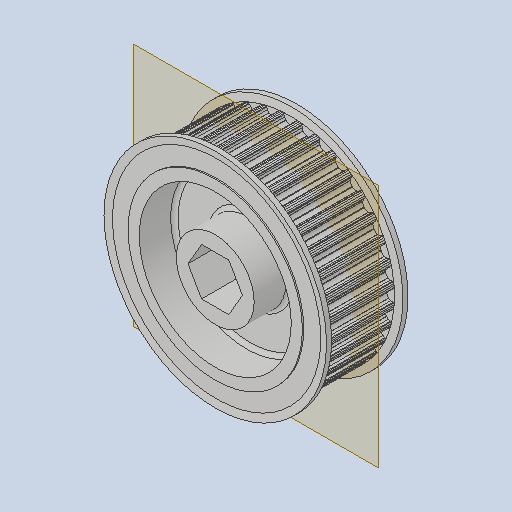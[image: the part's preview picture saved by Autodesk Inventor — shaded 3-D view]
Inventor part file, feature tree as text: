
AUTODESK INVENTOR PART (.ipt)
format: ipt  version: 2023.4 (Build 274418000, 418)  size: 806,400 bytes
history: native  units: in
note: dims shown in document units (in); Inventor stores cm internally (conversion verified against a paired STEP export)
features: mirror x1
ambient origin geometry x8: Origin, YZ Plane, XZ Plane, XY Plane, X Axis, Y Axis, Z Axis, Center Point
bodies: Solid1 (feature_tree)
feature tree (1):
  mirror  "Mirror1"
